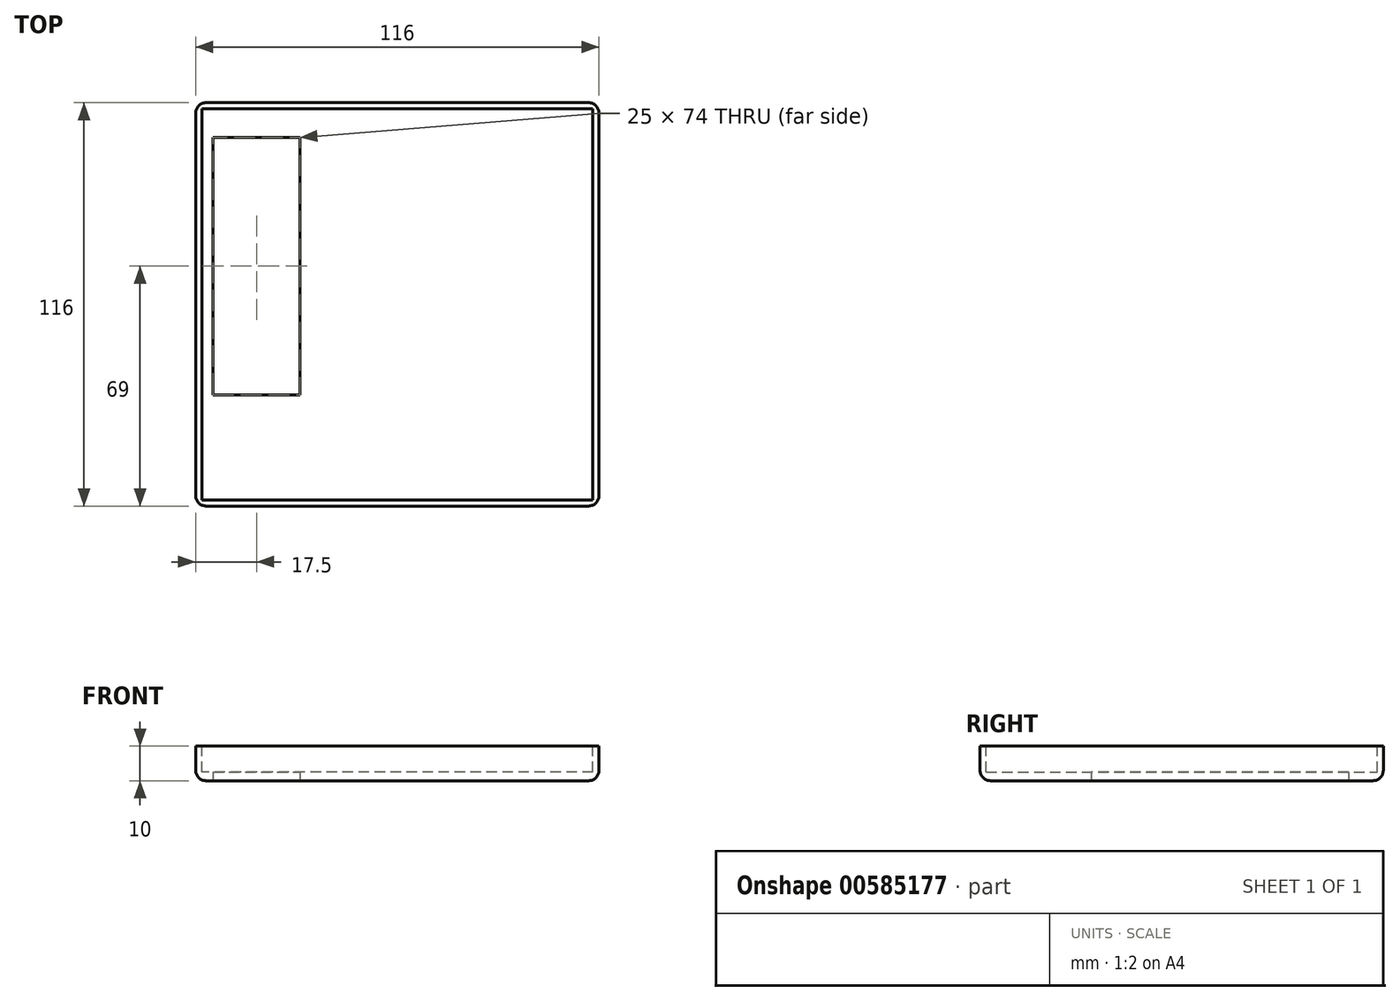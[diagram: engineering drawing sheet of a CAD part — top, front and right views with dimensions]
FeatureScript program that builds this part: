
annotation { "Feature Type Name" : "Feature", "Feature Type Description" : "" }
export const myFeature = defineFeature(function(context is Context, id is Id, definition is map)
    precondition{}
    {
        {
            var Q0;
            Q0=qCreatedBy(makeId("Top.planeOp"),FACE);
            var sketch = newSketch(context, id + "F0", { "sketchPlane" : qUnion([Q0])});
            skPoint(sketch, "E0.middle", {"position": v(0, 0) * mm});
            skLineSegment(sketch, "E1.bottom", {"start": v(58, -58) * mm, "end": v(-58, -58) * mm});
            skLineSegment(sketch, "E1.top", {"start": v(58, 58) * mm, "end": v(-58, 58) * mm});
            skLineSegment(sketch, "E1.left", {"start": v(58, -58) * mm, "end": v(58, 58) * mm});
            skLineSegment(sketch, "E1.right", {"start": v(-58, -58) * mm, "end": v(-58, 58) * mm});
            skLineSegment(sketch, "E2.bottom", {"start": v(-53, 48) * mm, "end": v(-28, 48) * mm});
            skLineSegment(sketch, "E2.top", {"start": v(-53, -26) * mm, "end": v(-28, -26) * mm});
            skLineSegment(sketch, "E2.left", {"start": v(-53, 48) * mm, "end": v(-53, -26) * mm});
            skLineSegment(sketch, "E2.right", {"start": v(-28, 48) * mm, "end": v(-28, -26) * mm});
            skSolve(sketch);
        }
        {
            var Q0;
            Q0=makeQuery(id+"F0.imprint","IMPRINT",FACE,{"disambiguationData":[TD([[makeQuery(id+"F0.imprint","IMPRINT",EDGE,{"derivedFrom":sQuery(id+"F0.wireOp",EDGE,"E1.bottom")}),-1.0]])]});
            extrude(context, id + "F1", {"entities" : qUnion([Q0]), "depth" : 10 * mm, "offsetDistance" : 25 * mm});
        }
        {
            var Q0;
            Q0=makeQuery(id+"F1.opExtrude","CAP_FACE",FACE,{"disambiguationData":[OSD([sQuery(id+"F0.wireOp",EDGE,"E1.bottom"),sQuery(id+"F0.wireOp",EDGE,"E1.top"),sQuery(id+"F0.wireOp",EDGE,"E1.left"),sQuery(id+"F0.wireOp",EDGE,"E1.right")])],"isStart":false});
            var sketch = newSketch(context, id + "F2", { "sketchPlane" : qUnion([Q0])});
            skLineSegment(sketch, "E3.bottom", {"start": v(56.25, -56.25) * mm, "end": v(-56.25, -56.25) * mm});
            skLineSegment(sketch, "E3.top", {"start": v(56.25, 56.25) * mm, "end": v(-56.25, 56.25) * mm});
            skLineSegment(sketch, "E3.left", {"start": v(56.25, -56.25) * mm, "end": v(56.25, 56.25) * mm});
            skLineSegment(sketch, "E3.right", {"start": v(-56.25, -56.25) * mm, "end": v(-56.25, 56.25) * mm});
            skPoint(sketch, "E3.middle", {"position": v(0, 0) * mm});
            skSolve(sketch);
        }
        {
            var Q0;
            Q0=makeQuery(id+"F2.imprint","IMPRINT",FACE,{"disambiguationData":[TD([[makeQuery(id+"F2.imprint","IMPRINT",EDGE,{"derivedFrom":sQuery(id+"F2.wireOp",EDGE,"E3.bottom")}),-1.0]])]});
            extrude(context, id + "F3", {"entities" : qUnion([Q0]), "operationType" : NewBodyOperationType.REMOVE, "oppositeDirection" : true, "depth" : 7.5 * mm, "offsetDistance" : 25 * mm});
        }
        {
            var Q0;
            Q0=makeQuery(id+"F1.opExtrude","SWEPT_EDGE",EDGE,{"disambiguationData":[OSD([sQuery(id+"F0.wireOp",EDGE,"E1.top"),sQuery(id+"F0.wireOp",EDGE,"E1.left")])]});
            var Q1;
            Q1=makeQuery(id+"F1.opExtrude","SWEPT_EDGE",EDGE,{"disambiguationData":[OSD([sQuery(id+"F0.wireOp",EDGE,"E1.bottom"),sQuery(id+"F0.wireOp",EDGE,"E1.left")])]});
            var Q2;
            Q2=makeQuery(id+"F1.opExtrude","SWEPT_EDGE",EDGE,{"disambiguationData":[OSD([sQuery(id+"F0.wireOp",EDGE,"E1.top"),sQuery(id+"F0.wireOp",EDGE,"E1.right")])]});
            var Q3;
            Q3=makeQuery(id+"F1.opExtrude","SWEPT_EDGE",EDGE,{"disambiguationData":[OSD([sQuery(id+"F0.wireOp",EDGE,"E1.bottom"),sQuery(id+"F0.wireOp",EDGE,"E1.right")])]});
            var Q4;
            Q4=makeQuery(id+"F1.opExtrude","CAP_EDGE",EDGE,{"disambiguationData":[OSD([sQuery(id+"F0.wireOp",EDGE,"E1.right")])],"isStart":true});
            var Q5;
            Q5=makeQuery(id+"F1.opExtrude","CAP_EDGE",EDGE,{"disambiguationData":[OSD([sQuery(id+"F0.wireOp",EDGE,"E1.bottom")])],"isStart":true});
            var Q6;
            Q6=makeQuery(id+"F1.opExtrude","CAP_EDGE",EDGE,{"disambiguationData":[OSD([sQuery(id+"F0.wireOp",EDGE,"E1.top")])],"isStart":true});
            var Q7;
            Q7=makeQuery(id+"F1.opExtrude","CAP_EDGE",EDGE,{"disambiguationData":[OSD([sQuery(id+"F0.wireOp",EDGE,"E1.left")])],"isStart":true});
            fillet(context, id + "F4", {"entities" : qUnion([Q0, Q1, Q2, Q3, Q4, Q5, Q6, Q7]), "radius" : 3 * mm, "tangentPropagation" : true, "allowEdgeOverflow" : false});
        }
    });
